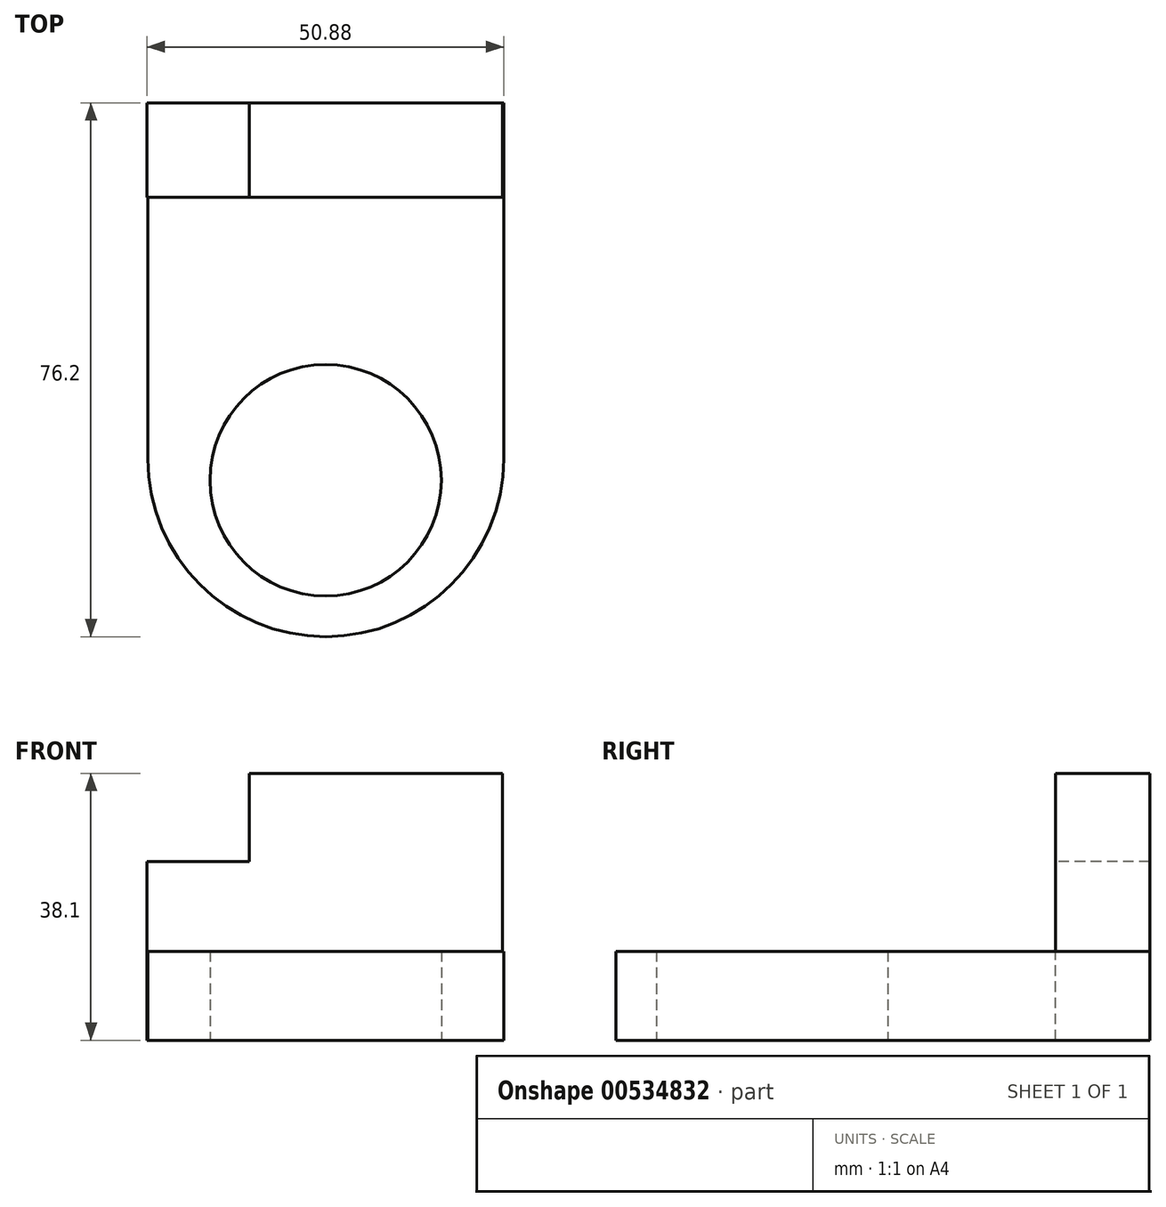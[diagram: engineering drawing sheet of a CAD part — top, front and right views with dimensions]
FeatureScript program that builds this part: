
annotation { "Feature Type Name" : "Feature", "Feature Type Description" : "" }
export const myFeature = defineFeature(function(context is Context, id is Id, definition is map)
    precondition{}
    {
        {
            var Q0;
            Q0=qCreatedBy(makeId("Top.planeOp"),FACE);
            var sketch = newSketch(context, id + "F0", { "sketchPlane" : qUnion([Q0])});
            skLineSegment(sketch, "E0.bottom", {"start": v(-25.4, 38.1) * mm, "end": v(25.4, 38.1) * mm});
            skLineSegment(sketch, "E0.top", {"start": v(-25.4, -38.1) * mm, "end": v(25.4, -38.1) * mm});
            skLineSegment(sketch, "E0.left", {"start": v(-25.4, 38.1) * mm, "end": v(-25.4, -38.1) * mm});
            skLineSegment(sketch, "E0.right", {"start": v(25.4, 38.1) * mm, "end": v(25.4, -38.1) * mm});
            skPoint(sketch, "E0.middle", {"position": v(0, 0) * mm});
            skSolve(sketch);
        }
        {
            var Q0;
            Q0=makeQuery(id+"F0.imprint","IMPRINT",FACE,{"disambiguationData":[TD([[makeQuery(id+"F0.imprint","IMPRINT",EDGE,{"derivedFrom":sQuery(id+"F0.wireOp",EDGE,"E0.bottom")}),-1.0]])]});
            extrude(context, id + "F1", {"entities" : qUnion([Q0]), "depth" : 12.7 * mm, "offsetDistance" : 25.4 * mm});
        }
        {
            var Q0;
            Q0=makeQuery(id+"F1.opExtrude","SWEPT_EDGE",EDGE,{"disambiguationData":[OSD([sQuery(id+"F0.wireOp",EDGE,"E0.top"),sQuery(id+"F0.wireOp",EDGE,"E0.right")])]});
            fillet(context, id + "F2", {"entities" : qUnion([Q0]), "radius" : 25.4 * mm, "tangentPropagation" : true, "allowEdgeOverflow" : false});
        }
        {
            var Q0;
            Q0=makeQuery(id+"F1.opExtrude","SWEPT_EDGE",EDGE,{"disambiguationData":[OSD([sQuery(id+"F0.wireOp",EDGE,"E0.top"),sQuery(id+"F0.wireOp",EDGE,"E0.left")])]});
            fillet(context, id + "F3", {"entities" : qUnion([Q0]), "radius" : 25.4 * mm, "tangentPropagation" : true, "allowEdgeOverflow" : false});
        }
        {
            var Q0;
            Q0=qCreatedBy(makeId("Top.planeOp"),FACE);
            var sketch = newSketch(context, id + "F4", { "sketchPlane" : qUnion([Q0])});
            skLineSegment(sketch, "E1.bottom", {"start": v(-25.48, 38.1) * mm, "end": v(25.24, 38.1) * mm});
            skLineSegment(sketch, "E1.top", {"start": v(-25.48, 24.63) * mm, "end": v(25.24, 24.63) * mm});
            skLineSegment(sketch, "E1.left", {"start": v(-25.48, 38.1) * mm, "end": v(-25.48, 24.63) * mm});
            skLineSegment(sketch, "E1.right", {"start": v(25.24, 38.1) * mm, "end": v(25.24, 24.63) * mm});
            skSolve(sketch);
        }
        {
            var Q0;
            Q0=makeQuery(id+"F4.imprint","IMPRINT",FACE,{"disambiguationData":[TD([[makeQuery(id+"F4.imprint","IMPRINT",EDGE,{"derivedFrom":sQuery(id+"F4.wireOp",EDGE,"E1.bottom")}),-1.0]])]});
            extrude(context, id + "F5", {"entities" : qUnion([Q0]), "operationType" : NewBodyOperationType.ADD, "depth" : 38.1 * mm, "offsetDistance" : 25.4 * mm});
        }
        {
            var Q0;
            Q0=makeQuery(id+"F5.opExtrude","SWEPT_FACE",FACE,{"disambiguationData":[OSD([sQuery(id+"F4.wireOp",EDGE,"E1.top")])]});
            var sketch = newSketch(context, id + "F6", { "sketchPlane" : qUnion([Q0])});
            skLineSegment(sketch, "E2.bottom", {"start": v(-25.48, 38.1) * mm, "end": v(-10.9, 38.1) * mm});
            skLineSegment(sketch, "E2.top", {"start": v(-25.48, 25.5) * mm, "end": v(-10.9, 25.5) * mm});
            skLineSegment(sketch, "E2.left", {"start": v(-25.48, 38.1) * mm, "end": v(-25.48, 25.5) * mm});
            skLineSegment(sketch, "E2.right", {"start": v(-10.9, 38.1) * mm, "end": v(-10.9, 25.5) * mm});
            skSolve(sketch);
        }
        {
            var Q0;
            Q0=makeQuery(id+"F6.imprint","IMPRINT",FACE,{"disambiguationData":[TD([[makeQuery(id+"F6.imprint","IMPRINT",EDGE,{"derivedFrom":sQuery(id+"F6.wireOp",EDGE,"E2.bottom")}),-1.0]])]});
            extrude(context, id + "F7", {"entities" : qUnion([Q0]), "operationType" : NewBodyOperationType.REMOVE, "endBound" : BoundingType.THROUGH_ALL, "oppositeDirection" : true, "depth" : 25.4 * mm, "offsetDistance" : 25.4 * mm});
        }
        {
            var Q0;
            Q0=qCreatedBy(makeId("Top.planeOp"),FACE);
            var sketch = newSketch(context, id + "F8", { "sketchPlane" : qUnion([Q0])});
            skCircle(sketch, "E3", {"center": v(0, -15.78) * mm, "radius": 16.51 * mm});
            skSolve(sketch);
        }
        {
            var Q0;
            Q0=makeQuery(id+"F8.imprint","IMPRINT",FACE,{"disambiguationData":[TD([[makeQuery(id+"F8.imprint","IMPRINT",EDGE,{"derivedFrom":sQuery(id+"F8.wireOp",EDGE,"E3")}),1.0]])]});
            extrude(context, id + "F9", {"entities" : qUnion([Q0]), "operationType" : NewBodyOperationType.REMOVE, "endBound" : BoundingType.THROUGH_ALL, "depth" : 25.4 * mm, "offsetDistance" : 25.4 * mm});
        }
    });
